# Revit family: IS_Ceratherm50_A5550_BIM_CZ
name_source: partatom
category: Plumbing Fixtures
revit_build: Autodesk Revit 2015 (Build: 20140606_1530(x64)
units: mm (PartAtom-declared; Revit-internal decimal feet)

## types (1)
- A5550AA - CERATHERM 50 VANOVA BATERIE TERMOSTATICKA NASTENNA
    Assembly Code = C1030200
    Barva = chrom
    Cárový kód = 4015413314466
    Default Elevation = 1219 mm
    Description = CERATHERM 50 VANOVA BATERIE TERMOSTATICKA NASTENNA
    Doba trvání zákonné záruky = 2
    Druh exportu IFC = Sanitary terminal
    Druh ventilu = 0
    Délka = 191 mm
    Hloubka = 0 mm  [stored 0 ft]
    Hmotnost netto = 2.82
    IFC export jako = Vodovodní baterie
    Informace o záruce = www.idealstandard.cz
    Instalacní návod = www.idealstandard.cz/servis-a-podpora
    Jednotka objemu = L
    Materiál = mosaz
    Mechanizmus ventilu = termostatická kartuše
    Model = A5550AA
    Náhradní náklady = 0 $
    Pomoc = www.idealstandard.cz
    Popis baterie = Ideal Standard
    Povrch = chrom
    Predpokládaná životnost = 25
    Prutok = 21/13L/min @ 3bar
    Specifikace = Vanová termostatická baterie nástěnná (DN 15) se zařízením na zamezení zpětného toku. 100% Cool Body technologie. Perlátor. Vývod 173 mm. Skryté S-přípojky s nízkou hlučností (nastavitelné od 137 - 163 mm). Kovová nástěnná rozeta s těsněním. Automatický přepínač ze sprchy do vany. Kartuše s keramickými disky. Regulace teploty s ochranou proti opaření. Omezovač teploty (dětská pojistka). Blokovací Eco tlačítko k omezení průtoku vody. Ochrana proti hluku DIN 4109, třída 1.
    Standardizace = EN 817, DIN 4109
    Telefon = 606640445
    Tvar = zaoblený
    Typ baterie = nástěnná
    Typ montáže = instalace
    URL = www.idealstandard.cz
    Velikost = 303 x 70 x 191 mm
    Verze Uniclass 2015 = Products v1.1
    Výrobce = Ideal Standard s.r.o.
    Výška = 70 mm
    Znacka = Ideal Standard
    Zárucní doba = rok
    Zárucní doba výrobku = 5
    Záruka = Záruka výrobce
    web výrobce = www.idealstandard.cz
    Šírka = 303 mm

note: [stored X ft] marks values corroborated as IEEE doubles in the binary element streams (Revit-internal decimal feet)

## geometry (parser evidence)
native form markers: Blend x4, Sweep x1
no freeform markers — native parametric forms only
